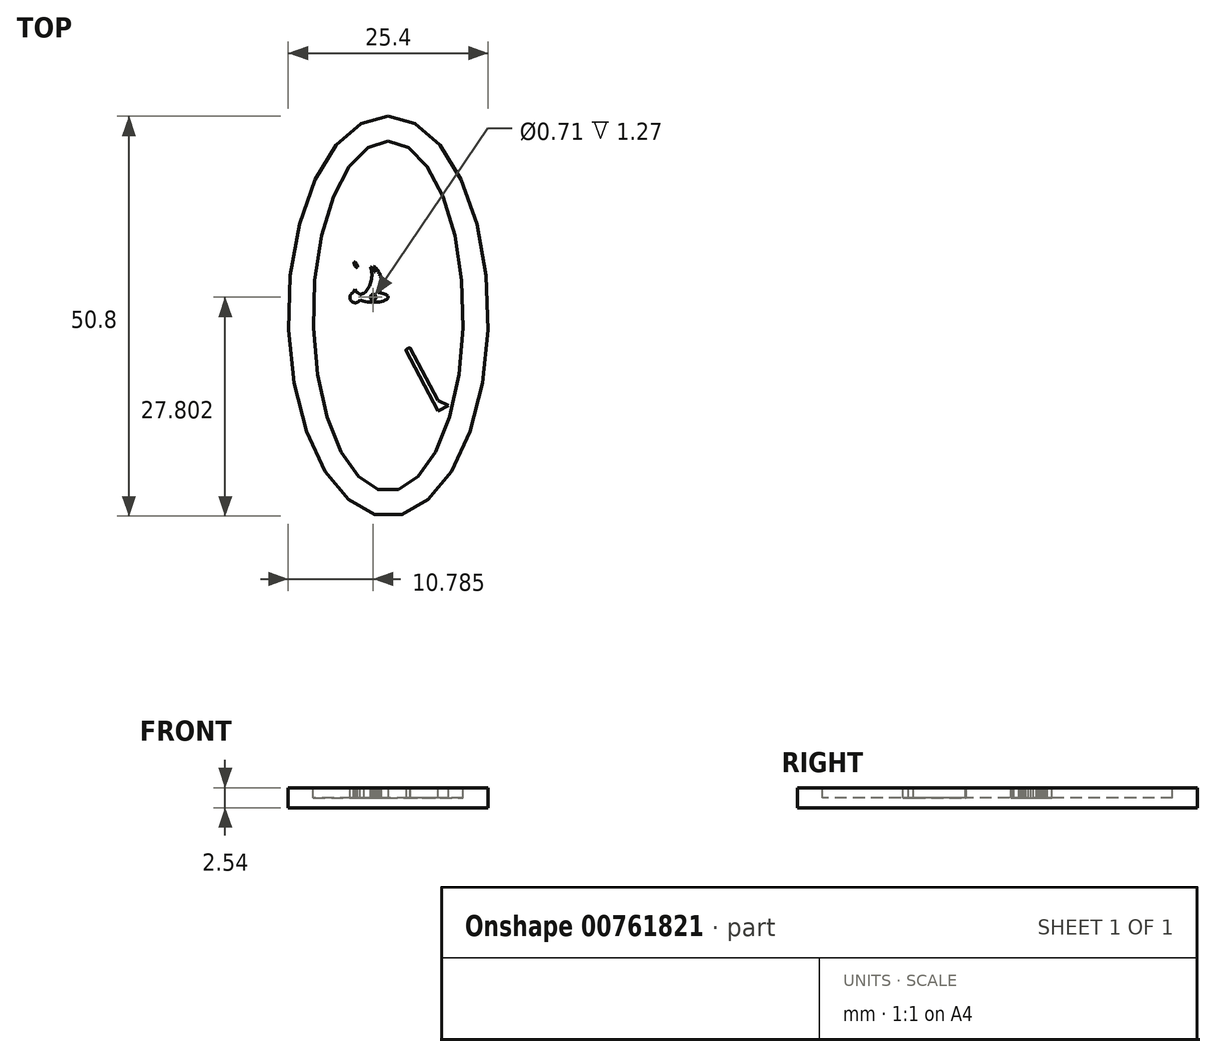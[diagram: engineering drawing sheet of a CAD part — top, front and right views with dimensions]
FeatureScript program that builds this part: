
annotation { "Feature Type Name" : "Feature", "Feature Type Description" : "" }
export const myFeature = defineFeature(function(context is Context, id is Id, definition is map)
    precondition{}
    {
        {
            var Q0;
            Q0=qCreatedBy(makeId("Top.planeOp"),FACE);
            var sketch = newSketch(context, id + "F0", { "sketchPlane" : qUnion([Q0])});
            skEllipse(sketch, "E0", {"center": v(0, 0) * mm, "majorRadius": 25.4 * mm, "minorRadius": 12.7 * mm, "majorAxis": v(0, 1)});
            skSolve(sketch);
        }
        {
            var Q0;
            Q0=qSketchRegion(id+"F0",true);
            extrude(context, id + "F1", {"entities" : qUnion([Q0]), "depth" : 2.54 * mm, "offsetDistance" : 25.4 * mm});
        }
        {
            var Q0;
            Q0=makeQuery(id+"F1.opExtrude","CAP_FACE",FACE,{"disambiguationData":[OSD([sQuery(id+"F0.wireOp",EDGE,"E0")])],"isStart":false});
            var sketch = newSketch(context, id + "F2", { "sketchPlane" : qUnion([Q0])});
            skEllipse(sketch, "E1", {"center": v(0, 0) * mm, "majorRadius": 22.23 * mm, "minorRadius": 9.53 * mm, "majorAxis": v(0, 1)});
            skSolve(sketch);
        }
        {
            var Q0;
            Q0=qSketchRegion(id+"F2",true);
            extrude(context, id + "F3", {"entities" : qUnion([Q0]), "operationType" : NewBodyOperationType.REMOVE, "oppositeDirection" : true, "depth" : 1.27 * mm, "offsetDistance" : 25.4 * mm});
        }
        {
            var Q0;
            Q0=makeQuery(id+"F2.imprint","IMPRINT",FACE,{"disambiguationData":[TD([[makeQuery(id+"F2.imprint","IMPRINT",EDGE,{"derivedFrom":sQuery(id+"F2.wireOp",EDGE,"E1")}),1.0]])]});
            var sketch = newSketch(context, id + "F4", { "sketchPlane" : qUnion([Q0])});
            skCircle(sketch, "E2", {"center": v(-4.19, 2.38) * mm, "radius": 0.68 * mm});
            skEllipse(sketch, "E3", {"center": v(-1.91, 2.4) * mm, "majorRadius": 1.9 * mm, "minorRadius": 0.64 * mm, "majorAxis": v(-1, 0)});
            skArc(sketch, "E4", {"start": v(-2.67, 3) * mm, "mid": v(-1.78, 4.54) * mm, "end": v(-1.85, 6.33) * mm});
            skArc(sketch, "E5", {"start": v(-1.2, 3) * mm, "mid": v(-1, 4.77) * mm, "end": v(-1.85, 6.33) * mm});
            skLineSegment(sketch, "E6", {"start": v(-4.4, 3.03) * mm, "end": v(-4.23, 3.42) * mm});
            skLineSegment(sketch, "E7", {"start": v(-4.23, 3.42) * mm, "end": v(-4.1, 3.06) * mm});
            skArc(sketch, "E8", {"start": v(-1.2, 3) * mm, "mid": v(-1.05, 3.1) * mm, "end": v(-1.09, 3.3) * mm});
            skArc(sketch, "E9", {"start": v(-1.09, 3.3) * mm, "mid": v(-0.95, 3.42) * mm, "end": v(-1, 3.6) * mm});
            skArc(sketch, "E10", {"start": v(-1, 3.6) * mm, "mid": v(-0.87, 3.73) * mm, "end": v(-0.96, 3.9) * mm});
            skArc(sketch, "E11", {"start": v(-0.96, 3.9) * mm, "mid": v(-0.82, 4.07) * mm, "end": v(-0.94, 4.26) * mm});
            skArc(sketch, "E12", {"start": v(-0.94, 4.26) * mm, "mid": v(-0.82, 4.42) * mm, "end": v(-0.96, 4.57) * mm});
            skArc(sketch, "E13", {"start": v(-0.96, 4.57) * mm, "mid": v(-0.86, 4.76) * mm, "end": v(-1.02, 4.9) * mm});
            skArc(sketch, "E14", {"start": v(-1.02, 4.9) * mm, "mid": v(-0.94, 5.08) * mm, "end": v(-1.1, 5.18) * mm});
            skArc(sketch, "E15", {"start": v(-1.1, 5.18) * mm, "mid": v(-1.02, 5.36) * mm, "end": v(-1.21, 5.44) * mm});
            skArc(sketch, "E16", {"start": v(-1.21, 5.44) * mm, "mid": v(-1.18, 5.61) * mm, "end": v(-1.34, 5.69) * mm});
            skArc(sketch, "E17", {"start": v(-1.34, 5.69) * mm, "mid": v(-1.33, 5.85) * mm, "end": v(-1.48, 5.9) * mm});
            skArc(sketch, "E18", {"start": v(-1.48, 5.9) * mm, "mid": v(-1.47, 6.04) * mm, "end": v(-1.6, 6.07) * mm});
            skArc(sketch, "E19", {"start": v(-1.6, 6.07) * mm, "mid": v(-1.62, 6.2) * mm, "end": v(-1.74, 6.22) * mm});
            skArc(sketch, "E20", {"start": v(-3.06, 2.91) * mm, "mid": v(-2.16, 4.47) * mm, "end": v(-2.24, 6.26) * mm});
            skArc(sketch, "E21", {"start": v(-1.45, 5.03) * mm, "mid": v(-1.77, 5.7) * mm, "end": v(-2.24, 6.26) * mm});
            skArc(sketch, "E22", {"start": v(-1.74, 5.6) * mm, "mid": v(-1.72, 5.77) * mm, "end": v(-1.87, 5.82) * mm});
            skArc(sketch, "E23", {"start": v(-1.87, 5.82) * mm, "mid": v(-1.87, 5.96) * mm, "end": v(-2, 6) * mm});
            skArc(sketch, "E24", {"start": v(-2, 6) * mm, "mid": v(-2.02, 6.11) * mm, "end": v(-2.13, 6.14) * mm});
            skCircle(sketch, "E25", {"center": v(-1.91, 2.4) * mm, "radius": 0.36 * mm});
            skFitSpline(sketch, "E26", {"points": [v(-4.3, 6.87) * mm, v(-4.32, 6.69) * mm, v(-4.07, 6.2) * mm, v(-3.92, 6.25) * mm, v(-4.1, 6.71) * mm, v(-4.3, 6.87) * mm]});
            skEllipse(sketch, "E27", {"center": v(2.52, -4.2) * mm, "majorRadius": 0.32 * mm, "minorRadius": 0.08 * mm, "majorAxis": v(0.88, 0.47)});
            skLineSegment(sketch, "E28", {"start": v(2.24, -4.34) * mm, "end": v(6.32, -12.02) * mm});
            skLineSegment(sketch, "E29", {"start": v(6.32, -12.02) * mm, "end": v(7.64, -11.32) * mm});
            skLineSegment(sketch, "E30", {"start": v(7.64, -11.32) * mm, "end": v(6.32, -10.7) * mm});
            skLineSegment(sketch, "E31", {"start": v(6.32, -10.7) * mm, "end": v(2.8, -4.07) * mm});
            skPoint(sketch, "E31.endSnap0", {"position": v(2.8, -4.04) * mm});
            skSolve(sketch);
        }
        {
            var Q0;
            Q0=qSketchRegion(id+"F4",true);
            extrude(context, id + "F5", {"entities" : qUnion([Q0]), "operationType" : NewBodyOperationType.ADD, "oppositeDirection" : true, "depth" : 1.27 * mm, "offsetDistance" : 25.4 * mm});
        }
    });
